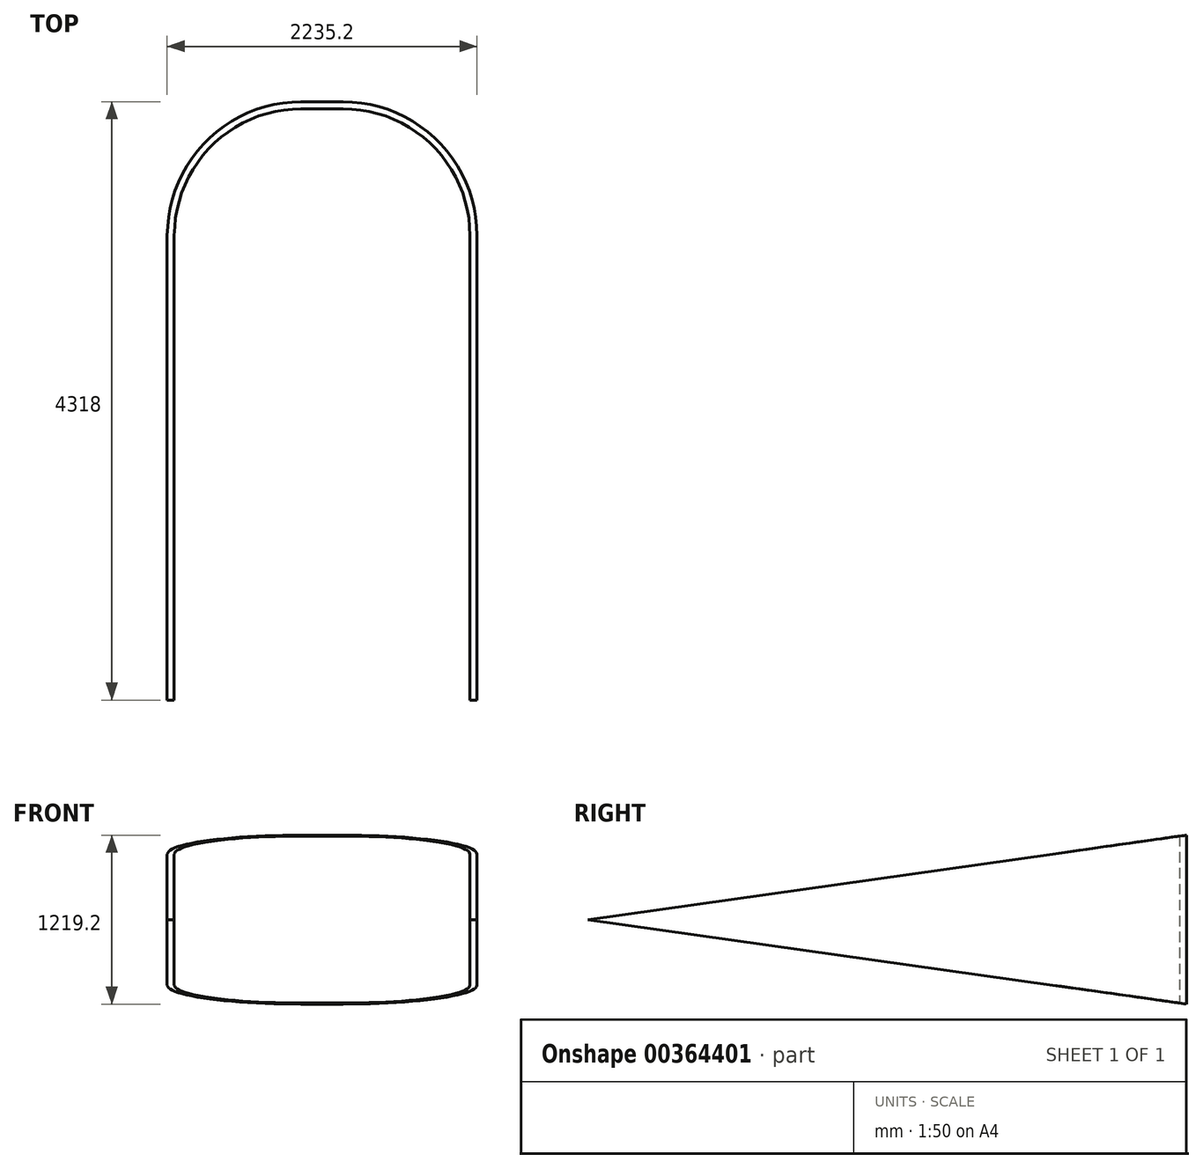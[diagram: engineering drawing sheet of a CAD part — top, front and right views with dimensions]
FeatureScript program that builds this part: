
annotation { "Feature Type Name" : "Feature", "Feature Type Description" : "" }
export const myFeature = defineFeature(function(context is Context, id is Id, definition is map)
    precondition{}
    {
        {
            var Q0;
            Q0=qCreatedBy(makeId("Top.planeOp"),FACE);
            var sketch = newSketch(context, id + "F0", { "sketchPlane" : qUnion([Q0])});
            skLineSegment(sketch, "E0.bottom", {"start": v(-107.95, 2133.6) * mm, "end": v(196.85, 2133.6) * mm});
            skLineSegment(sketch, "E0.left", {"start": v(-1022.35, 1219.2) * mm, "end": v(-1022.35, -2133.6) * mm});
            skLineSegment(sketch, "E0.right", {"start": v(1111.25, 1219.2) * mm, "end": v(1111.25, -2133.6) * mm});
            skArc(sketch, "E1.filletArc", {"start": v(-107.95, 2133.6) * mm, "mid": v(-754.53, 1865.78) * mm, "end": v(-1022.35, 1219.2) * mm});
            skArc(sketch, "E2.filletArc", {"start": v(1111.25, 1219.2) * mm, "mid": v(843.43, 1865.78) * mm, "end": v(196.85, 2133.6) * mm});
            skLineSegment(sketch, "E3.0", {"start": v(-1073.15, 1219.2) * mm, "end": v(-1073.15, -2133.6) * mm});
            skLineSegment(sketch, "E3.1", {"start": v(1162.05, 1219.2) * mm, "end": v(1162.05, -2133.6) * mm});
            skArc(sketch, "E3.2", {"start": v(1162.05, 1219.2) * mm, "mid": v(879.35, 1901.7) * mm, "end": v(196.85, 2184.4) * mm});
            skLineSegment(sketch, "E3.3", {"start": v(-107.95, 2184.4) * mm, "end": v(196.85, 2184.4) * mm});
            skArc(sketch, "E3.4", {"start": v(-107.95, 2184.4) * mm, "mid": v(-790.45, 1901.7) * mm, "end": v(-1073.15, 1219.2) * mm});
            skLineSegment(sketch, "E4", {"start": v(-1073.15, -2133.6) * mm, "end": v(-1022.35, -2133.6) * mm});
            skLineSegment(sketch, "E5", {"start": v(1111.25, -2133.6) * mm, "end": v(1162.05, -2133.6) * mm});
            skSolve(sketch);
        }
        {
            var Q0;
            Q0=qSketchRegion(id+"F0",true);
            extrude(context, id + "F1", {"entities" : qUnion([Q0]), "depth" : 1219.2 * mm});
        }
        {
            var Q0;
            Q0=makeQuery(id+"F1.opExtrude","SWEPT_FACE",FACE,{"disambiguationData":[OSD([sQuery(id+"F0.wireOp",EDGE,"E3.1")])]});
            var sketch = newSketch(context, id + "F2", { "sketchPlane" : qUnion([Q0])});
            skLineSegment(sketch, "E6", {"start": v(2184.4, 1219.2) * mm, "end": v(-2133.6, 1219.2) * mm});
            skLineSegment(sketch, "E7", {"start": v(-2133.6, 1219.2) * mm, "end": v(-2133.6, 609.6) * mm});
            skLineSegment(sketch, "E8", {"start": v(-2133.6, 609.6) * mm, "end": v(2184.4, 1219.2) * mm});
            skLineSegment(sketch, "E9", {"start": v(-2133.6, 609.6) * mm, "end": v(2184.4, 0) * mm});
            skLineSegment(sketch, "E10", {"start": v(2184.4, 0) * mm, "end": v(2184.4, 1219.2) * mm});
            skLineSegment(sketch, "E11", {"start": v(-2133.6, 609.6) * mm, "end": v(-2133.6, 0) * mm});
            skLineSegment(sketch, "E12", {"start": v(-2133.6, 0) * mm, "end": v(2184.4, 0) * mm});
            skSolve(sketch);
        }
        {
            var Q0;
            {var subQ4=sQuery(id+"F2.wireOp",EDGE,"E7");Q0=makeQuery(id+"F2.imprint","IMPRINT",FACE,{"disambiguationData":[TD([[makeQuery(id+"F2.imprint","IMPRINT",EDGE,{"derivedFrom":subQ4}),1.0]])]});}
            var Q1;
            {var subQ0=sQuery(id+"F2.wireOp",EDGE,"E6");var subQ1=makeQuery(id+"F1.opExtrude","SWEPT_EDGE",EDGE,{"disambiguationData":[OSD([sQuery(id+"F0.wireOp",EDGE,"E3.1"),sQuery(id+"F0.wireOp",EDGE,"E3.2")])]});var subQ2=makeQuery(id+"F2.imprint","INTERSECT",VERTEX,{"derivedFrom":[subQ1,subQ0]});Q1=makeQuery(id+"F2.imprint","IMPRINT",FACE,{"disambiguationData":[TD([[makeQuery(id+"F2.imprint","IMPRINT",EDGE,{"disambiguationData":[TD([[subQ2,1.0]])],"derivedFrom":subQ0}),1.0]])]});}
            var Q2;
            {var subQ1=sQuery(id+"F0.wireOp",EDGE,"E3.1");var subQ6=makeQuery(id+"F1.opExtrude","CAP_EDGE",EDGE,{"disambiguationData":[OSD([subQ1])],"isStart":true});Q2=makeQuery(id+"F2.imprint","IMPRINT",FACE,{"disambiguationData":[TD([[makeQuery(id+"F2.imprint","IMPRINT",EDGE,{"derivedFrom":subQ6}),-1.0]])]});}
            var Q3;
            {var subQ0=sQuery(id+"F2.wireOp",EDGE,"E11");Q3=makeQuery(id+"F2.imprint","IMPRINT",FACE,{"disambiguationData":[TD([[makeQuery(id+"F2.imprint","IMPRINT",EDGE,{"derivedFrom":subQ0}),1.0]])]});}
            var Q4;
            {var subQ0=sQuery(id+"F2.wireOp",EDGE,"E12");var subQ1=sQuery(id+"F2.wireOp",EDGE,"E9");var subQ2=makeQuery(id+"F2.imprint","INTERSECT",VERTEX,{"derivedFrom":[subQ1,sQuery(id+"F2.wireOp",EDGE,"E10"),subQ0]});Q4=makeQuery(id+"F2.imprint","IMPRINT",FACE,{"disambiguationData":[TD([[makeQuery(id+"F2.imprint","IMPRINT",EDGE,{"disambiguationData":[TD([[subQ2,1.0]])],"derivedFrom":subQ1}),-1.0]])]});}
            extrude(context, id + "F3", {"entities" : qUnion([Q0, Q1, Q2, Q3, Q4]), "operationType" : NewBodyOperationType.REMOVE, "endBound" : BoundingType.THROUGH_ALL, "oppositeDirection" : true, "depth" : 25.4 * mm});
        }
    });
